# Revit family: SH-439-10W
name_source: partatom
category: Lighting Fixtures
revit_build: Autodesk Revit 2017 (Build: 20160225_1515(x64)
units: mm (PartAtom-declared; Revit-internal decimal feet)

## family parameters
Always vertical = No
Cut with Voids When Loaded = No
Light Source = No
OmniClass Number = 23.80.70.00
OmniClass Title = Lighting
Part Type = Normal
Room Calculation Point = No
Round Connector Dimension = Use Diameter
Shared = Yes
Work Plane-Based = Yes

## types (6) — shared parameters
Body Material = Aluminum
Default Elevation = 121.9 cm
Diameter = 4.5 cm
Diffuser = light
Height = 16.8 cm
IP = IP20
Manufacturer = SHOA
Protection Class = Class I
URL = https://www.shoaco.com
Website = www.shoaco.com
color rendering index(CRI) = 80<
consumption current = 0 A

## per-type parameters (varying)
| type | 3000K | 4000K | Body color | Flicker | LUMINAIRE | Lamp | Model | RAIL-1m | RAIL-2m | Type medule | Voltage/Frequency | color temperature | wattage |
| Sh-449(White color-3000K-LED) | Yes | No | White color1 | Free Flicker | Yes | LED | SH-449 | No | No | COB | 230V/50HZ | 3000K | 10 W |
| Sh-449(White color-4000K-LED) | No | Yes | White color1 | Free Flicker | Yes | LED | SH-449 | No | No | COB | 230V/50HZ | 4000K | 10 W |
| Sh-449(Black color-3000K-LED) | Yes | No | Black color | Free Flicker | Yes | LED | SH-449 | No | No | COB | 230V/50HZ | 3000K | 10 W |
| Sh-449(Black color-4000K-LED) | No | Yes | Black color | Free Flicker | Yes | LED | SH-449 | No | No | COB | 230V/50HZ | 4000K | 10 W |
| Sh-Track-1m | No | No | Black color |  | No |  | SH-Track-1m | Yes | No |  | 0 | 3000K | 0 W |
| Sh-Track-2m | No | No | Black color |  | No |  | SH-Track-2m | No | Yes |  | 0 | 3000K | 0 W |

## geometry (parser evidence)
native form markers: Sweep x12
no freeform markers — native parametric forms only
